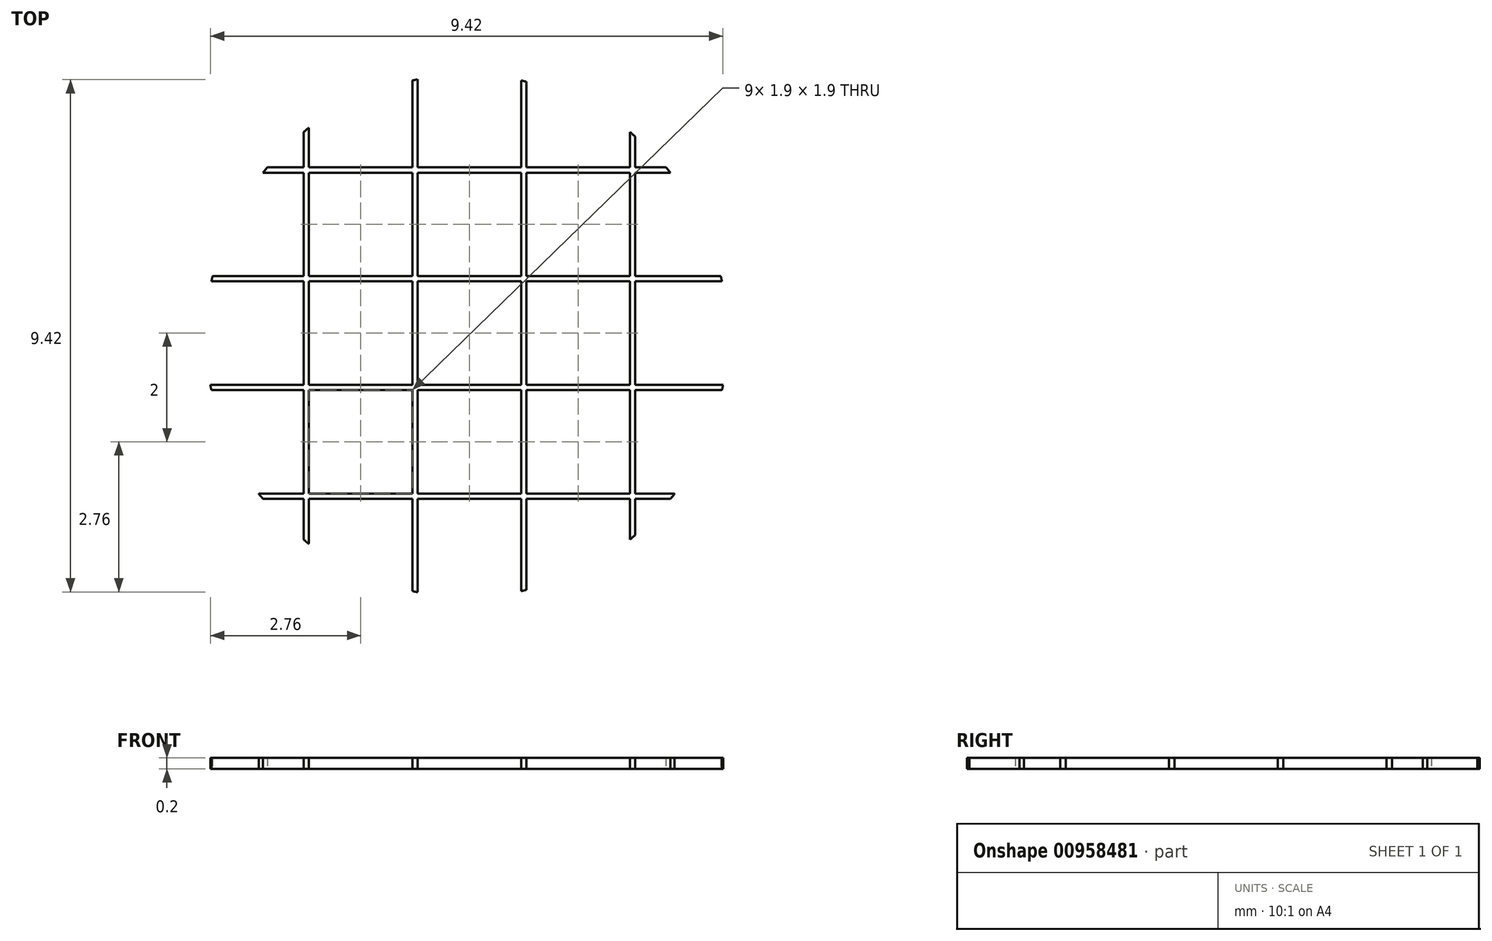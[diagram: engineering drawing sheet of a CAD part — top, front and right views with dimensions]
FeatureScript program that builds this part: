
annotation { "Feature Type Name" : "Feature", "Feature Type Description" : "" }
export const myFeature = defineFeature(function(context is Context, id is Id, definition is map)
    precondition{}
    {
        {
            var Q0;
            Q0=qCreatedBy(makeId("Top.planeOp"),FACE);
            var sketch = newSketch(context, id + "F0", { "sketchPlane" : qUnion([Q0])});
            skPoint(sketch, "E0.middle", {"position": v(0, 0) * mm});
            skArc(sketch, "E1", {"start": v(-3, 3.75) * mm, "mid": v(-3.35, 3.44) * mm, "end": v(-3.66, 3.1) * mm});
            skLineSegment(sketch, "E2.trimOffspring", {"start": v(-2.9, 3.82) * mm, "end": v(-2.9, 3.1) * mm});
            skLineSegment(sketch, "E3.trimOffspring", {"start": v(-3, 3.75) * mm, "end": v(-3, 3.1) * mm});
            skLineSegment(sketch, "E4.trimOffspring", {"start": v(-3, 3.1) * mm, "end": v(-3.66, 3.1) * mm});
            skLineSegment(sketch, "E5.trimOffspring", {"start": v(-3, 3) * mm, "end": v(-3.75, 3) * mm});
            skLineSegment(sketch, "E6.trimOffspring", {"start": v(-3, 3) * mm, "end": v(-3, 1.1) * mm});
            skLineSegment(sketch, "E7.trimOffspring", {"start": v(-2.9, 3) * mm, "end": v(-2.9, 1.1) * mm});
            skArc(sketch, "E8.trimOffspring", {"start": v(-3.75, 3) * mm, "mid": v(-4.32, 2.1) * mm, "end": v(-4.67, 1.1) * mm});
            skArc(sketch, "E9.trimOffspring", {"start": v(-4.7, 1) * mm, "mid": v(-4.8, 0.05) * mm, "end": v(-4.71, -0.9) * mm});
            skLineSegment(sketch, "E10.trimOffspring", {"start": v(-3, 1) * mm, "end": v(-3, -0.9) * mm});
            skLineSegment(sketch, "E11.trimOffspring", {"start": v(-3, 1.1) * mm, "end": v(-4.67, 1.1) * mm});
            skLineSegment(sketch, "E12.trimOffspring", {"start": v(-2.9, 1) * mm, "end": v(-2.9, -0.9) * mm});
            skLineSegment(sketch, "E13.trimOffspring", {"start": v(-3, 1) * mm, "end": v(-4.7, 1) * mm});
            skLineSegment(sketch, "E14.trimOffspring", {"start": v(-1, 3.1) * mm, "end": v(-2.9, 3.1) * mm});
            skLineSegment(sketch, "E15.trimOffspring", {"start": v(-1, 3) * mm, "end": v(-2.9, 3) * mm});
            skLineSegment(sketch, "E16.trimOffspring", {"start": v(-1, 3) * mm, "end": v(-1, 1.1) * mm});
            skLineSegment(sketch, "E17.trimOffspring", {"start": v(-0.9, 3) * mm, "end": v(-0.9, 1.1) * mm});
            skArc(sketch, "E18.trimOffspring", {"start": v(-1, 4.7) * mm, "mid": v(-2, 4.36) * mm, "end": v(-2.9, 3.82) * mm});
            skLineSegment(sketch, "E19.trimOffspring", {"start": v(-0.9, 4.71) * mm, "end": v(-0.9, 3.1) * mm});
            skLineSegment(sketch, "E20.trimOffspring", {"start": v(-1, 4.7) * mm, "end": v(-1, 3.1) * mm});
            skLineSegment(sketch, "E21.trimOffspring", {"start": v(1, 3.1) * mm, "end": v(-0.9, 3.1) * mm});
            skLineSegment(sketch, "E22.trimOffspring", {"start": v(1, 3) * mm, "end": v(1, 1.1) * mm});
            skLineSegment(sketch, "E23.trimOffspring", {"start": v(1, 3) * mm, "end": v(-0.9, 3) * mm});
            skLineSegment(sketch, "E24.trimOffspring", {"start": v(1.1, 3) * mm, "end": v(1.1, 1.1) * mm});
            skArc(sketch, "E25.trimOffspring", {"start": v(1, 4.7) * mm, "mid": v(0.05, 4.8) * mm, "end": v(-0.9, 4.71) * mm});
            skLineSegment(sketch, "E26.trimOffspring", {"start": v(1, 4.7) * mm, "end": v(1, 3.1) * mm});
            skLineSegment(sketch, "E27.trimOffspring", {"start": v(1.1, 4.67) * mm, "end": v(1.1, 3.1) * mm});
            skLineSegment(sketch, "E28.trimOffspring", {"start": v(-1, 1.1) * mm, "end": v(-2.9, 1.1) * mm});
            skLineSegment(sketch, "E29.trimOffspring", {"start": v(-1, 1) * mm, "end": v(-2.9, 1) * mm});
            skLineSegment(sketch, "E30.trimOffspring", {"start": v(-1, 1) * mm, "end": v(-1, -0.9) * mm});
            skLineSegment(sketch, "E31.trimOffspring", {"start": v(-0.9, 1) * mm, "end": v(-0.9, -0.9) * mm});
            skLineSegment(sketch, "E32.trimOffspring", {"start": v(1, 1.1) * mm, "end": v(-0.9, 1.1) * mm});
            skLineSegment(sketch, "E33.trimOffspring", {"start": v(1, 1) * mm, "end": v(1, -0.9) * mm});
            skLineSegment(sketch, "E34.trimOffspring", {"start": v(1, 1) * mm, "end": v(-0.9, 1) * mm});
            skLineSegment(sketch, "E35.trimOffspring", {"start": v(1.1, 1) * mm, "end": v(1.1, -0.9) * mm});
            skLineSegment(sketch, "E36.trimOffspring", {"start": v(3, 1.1) * mm, "end": v(1.1, 1.1) * mm});
            skLineSegment(sketch, "E37.trimOffspring", {"start": v(3, 1) * mm, "end": v(3, -0.9) * mm});
            skLineSegment(sketch, "E38.trimOffspring", {"start": v(3, 1) * mm, "end": v(1.1, 1) * mm});
            skLineSegment(sketch, "E39.trimOffspring", {"start": v(3.1, 1) * mm, "end": v(3.1, -0.9) * mm});
            skLineSegment(sketch, "E40.trimOffspring", {"start": v(3, 3) * mm, "end": v(1.1, 3) * mm});
            skLineSegment(sketch, "E41.trimOffspring", {"start": v(3, 3.1) * mm, "end": v(1.1, 3.1) * mm});
            skLineSegment(sketch, "E42.trimOffspring", {"start": v(3, 3) * mm, "end": v(3, 1.1) * mm});
            skLineSegment(sketch, "E43.trimOffspring", {"start": v(3.1, 3) * mm, "end": v(3.1, 1.1) * mm});
            skArc(sketch, "E44.trimOffspring", {"start": v(3, 3.75) * mm, "mid": v(2.1, 4.32) * mm, "end": v(1.1, 4.67) * mm});
            skLineSegment(sketch, "E45.trimOffspring", {"start": v(3, 3.75) * mm, "end": v(3, 3.1) * mm});
            skLineSegment(sketch, "E46.trimOffspring", {"start": v(3.1, 3.66) * mm, "end": v(3.1, 3.1) * mm});
            skLineSegment(sketch, "E47.trimOffspring", {"start": v(3.66, 3.1) * mm, "end": v(3.1, 3.1) * mm});
            skArc(sketch, "E48.trimOffspring", {"start": v(3.66, 3.1) * mm, "mid": v(3.4, 3.4) * mm, "end": v(3.1, 3.66) * mm});
            skLineSegment(sketch, "E49.trimOffspring", {"start": v(3.75, 3) * mm, "end": v(3.1, 3) * mm});
            skLineSegment(sketch, "E50.trimOffspring", {"start": v(4.67, 1.1) * mm, "end": v(3.1, 1.1) * mm});
            skArc(sketch, "E51.trimOffspring", {"start": v(4.67, 1.1) * mm, "mid": v(4.32, 2.1) * mm, "end": v(3.75, 3) * mm});
            skLineSegment(sketch, "E52.trimOffspring", {"start": v(4.7, 1) * mm, "end": v(3.1, 1) * mm});
            skLineSegment(sketch, "E53.trimOffspring", {"start": v(4.71, -0.9) * mm, "end": v(3.1, -0.9) * mm});
            skLineSegment(sketch, "E54.trimOffspring", {"start": v(4.7, -1) * mm, "end": v(3.1, -1) * mm});
            skArc(sketch, "E55.trimOffspring", {"start": v(4.71, -0.9) * mm, "mid": v(4.8, 0.05) * mm, "end": v(4.7, 1) * mm});
            skLineSegment(sketch, "E56.trimOffspring", {"start": v(3, -0.9) * mm, "end": v(1.1, -0.9) * mm});
            skLineSegment(sketch, "E57.trimOffspring", {"start": v(3.1, -1) * mm, "end": v(3.1, -2.9) * mm});
            skLineSegment(sketch, "E58.trimOffspring", {"start": v(3, -1) * mm, "end": v(1.1, -1) * mm});
            skLineSegment(sketch, "E59.trimOffspring", {"start": v(3, -1) * mm, "end": v(3, -2.9) * mm});
            skLineSegment(sketch, "E60.trimOffspring", {"start": v(1, -0.9) * mm, "end": v(-0.9, -0.9) * mm});
            skLineSegment(sketch, "E61.trimOffspring", {"start": v(1, -1) * mm, "end": v(-0.9, -1) * mm});
            skLineSegment(sketch, "E62.trimOffspring", {"start": v(1, -1) * mm, "end": v(1, -2.9) * mm});
            skLineSegment(sketch, "E63.trimOffspring", {"start": v(1.1, -1) * mm, "end": v(1.1, -2.9) * mm});
            skLineSegment(sketch, "E64.trimOffspring", {"start": v(-1, -1) * mm, "end": v(-2.9, -1) * mm});
            skLineSegment(sketch, "E65.trimOffspring", {"start": v(-1, -0.9) * mm, "end": v(-2.9, -0.9) * mm});
            skLineSegment(sketch, "E66.trimOffspring", {"start": v(-1, -1) * mm, "end": v(-1, -2.9) * mm});
            skLineSegment(sketch, "E67.trimOffspring", {"start": v(-0.9, -1) * mm, "end": v(-0.9, -2.9) * mm});
            skArc(sketch, "E68.trimOffspring", {"start": v(-4.7, -1) * mm, "mid": v(-4.36, -2) * mm, "end": v(-3.82, -2.9) * mm});
            skLineSegment(sketch, "E69.trimOffspring", {"start": v(-3, -0.9) * mm, "end": v(-4.71, -0.9) * mm});
            skLineSegment(sketch, "E70.trimOffspring", {"start": v(-3, -1) * mm, "end": v(-4.7, -1) * mm});
            skLineSegment(sketch, "E71.trimOffspring", {"start": v(-3, -1) * mm, "end": v(-3, -2.9) * mm});
            skLineSegment(sketch, "E72.trimOffspring", {"start": v(-2.9, -1) * mm, "end": v(-2.9, -2.9) * mm});
            skArc(sketch, "E73.trimOffspring", {"start": v(-3.75, -3) * mm, "mid": v(-3.4, -3.4) * mm, "end": v(-3, -3.75) * mm});
            skLineSegment(sketch, "E74.trimOffspring", {"start": v(-3, -3) * mm, "end": v(-3, -3.75) * mm});
            skLineSegment(sketch, "E75.trimOffspring", {"start": v(-3, -2.9) * mm, "end": v(-3.82, -2.9) * mm});
            skLineSegment(sketch, "E76.trimOffspring", {"start": v(-2.9, -3) * mm, "end": v(-2.9, -3.82) * mm});
            skLineSegment(sketch, "E77.trimOffspring", {"start": v(-3, -3) * mm, "end": v(-3.75, -3) * mm});
            skLineSegment(sketch, "E78.trimOffspring", {"start": v(-1, -3) * mm, "end": v(-1, -4.7) * mm});
            skLineSegment(sketch, "E79.trimOffspring", {"start": v(-1, -2.9) * mm, "end": v(-2.9, -2.9) * mm});
            skLineSegment(sketch, "E80.trimOffspring", {"start": v(-0.9, -3) * mm, "end": v(-0.9, -4.71) * mm});
            skLineSegment(sketch, "E81.trimOffspring", {"start": v(-1, -3) * mm, "end": v(-2.9, -3) * mm});
            skLineSegment(sketch, "E82.trimOffspring", {"start": v(1.1, -3) * mm, "end": v(1.1, -4.67) * mm});
            skLineSegment(sketch, "E83.trimOffspring", {"start": v(1, -2.9) * mm, "end": v(-0.9, -2.9) * mm});
            skLineSegment(sketch, "E84.trimOffspring", {"start": v(1, -3) * mm, "end": v(1, -4.7) * mm});
            skLineSegment(sketch, "E85.trimOffspring", {"start": v(1, -3) * mm, "end": v(-0.9, -3) * mm});
            skLineSegment(sketch, "E86.trimOffspring", {"start": v(3, -2.9) * mm, "end": v(1.1, -2.9) * mm});
            skLineSegment(sketch, "E87.trimOffspring", {"start": v(3, -3) * mm, "end": v(1.1, -3) * mm});
            skLineSegment(sketch, "E88.trimOffspring", {"start": v(3, -3) * mm, "end": v(3, -3.75) * mm});
            skLineSegment(sketch, "E89.trimOffspring", {"start": v(3.1, -3) * mm, "end": v(3.1, -3.66) * mm});
            skArc(sketch, "E90.trimOffspring", {"start": v(3.82, -2.9) * mm, "mid": v(4.36, -2) * mm, "end": v(4.7, -1) * mm});
            skLineSegment(sketch, "E91.trimOffspring", {"start": v(3.82, -2.9) * mm, "end": v(3.1, -2.9) * mm});
            skLineSegment(sketch, "E92.trimOffspring", {"start": v(3.75, -3) * mm, "end": v(3.1, -3) * mm});
            skArc(sketch, "E93.trimOffspring", {"start": v(3.1, -3.66) * mm, "mid": v(3.44, -3.35) * mm, "end": v(3.75, -3) * mm});
            skArc(sketch, "E94.trimOffspring", {"start": v(1.1, -4.67) * mm, "mid": v(2.1, -4.32) * mm, "end": v(3, -3.75) * mm});
            skArc(sketch, "E95.trimOffspring", {"start": v(-0.9, -4.71) * mm, "mid": v(0.05, -4.8) * mm, "end": v(1, -4.7) * mm});
            skArc(sketch, "E96.trimOffspring", {"start": v(-2.9, -3.82) * mm, "mid": v(-2, -4.36) * mm, "end": v(-1, -4.7) * mm});
            skCircle(sketch, "E97", {"center": v(0, 0) * mm, "radius": 4.8 * mm});
            skCircle(sketch, "E98", {"center": v(0, 0) * mm, "radius": 4.9 * mm});
            skSolve(sketch);
        }
        {
            var Q0;
            {var subQ17=sQuery(id+"F0.wireOp",EDGE,"E2.trimOffspring");Q0=makeQuery(id+"F0.imprint","IMPRINT",FACE,{"disambiguationData":[TD([[makeQuery(id+"F0.imprint","IMPRINT",EDGE,{"derivedFrom":subQ17}),-1.0]])]});}
            extrude(context, id + "F1", {"entities" : qUnion([Q0]), "depth" : .2 * mm, "offsetDistance" : 25 * mm});
        }
    });
